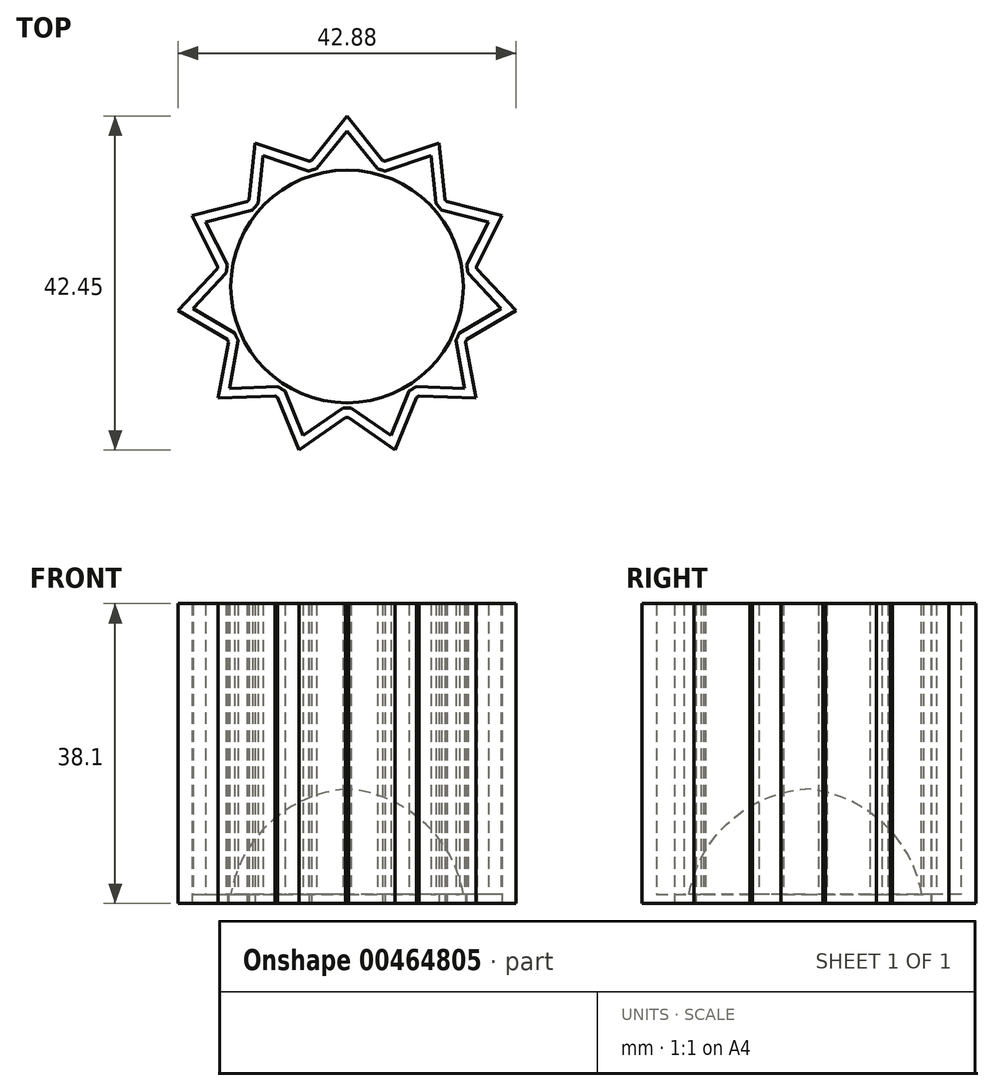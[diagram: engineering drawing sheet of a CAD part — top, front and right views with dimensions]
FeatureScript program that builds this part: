
annotation { "Feature Type Name" : "Feature", "Feature Type Description" : "" }
export const myFeature = defineFeature(function(context is Context, id is Id, definition is map)
    precondition{}
    {
        {
            var Q0;
            Q0=qCreatedBy(makeId("Top.planeOp"),FACE);
            var sketch = newSketch(context, id + "F0", { "sketchPlane" : qUnion([Q0])});
            skCircle(sketch, "E0", {"center": v(0, 0) * mm, "radius": 15.88 * mm, "construction": true});
            skCircle(sketch, "E1.0", {"center": v(0, 0) * mm, "radius": 16.64 * mm});
            skLineSegment(sketch, "E2", {"start": v(0, 0) * mm, "end": v(0, 21) * mm, "construction": true});
            skLineSegment(sketch, "E3", {"start": v(0, 21.66) * mm, "end": v(4.53, 16) * mm});
            skLineSegment(sketch, "E4.MirrorCS", {"start": v(0, 21.66) * mm, "end": v(-4.53, 16) * mm});
            skLineSegment(sketch, "E5.1.0", {"start": v(-11.71, 18.22) * mm, "end": v(-4.84, 15.92) * mm});
            skLineSegment(sketch, "E5.1.1", {"start": v(-11.71, 18.22) * mm, "end": v(-12.47, 11.02) * mm});
            skLineSegment(sketch, "E5.2.0", {"start": v(-19.7, 9) * mm, "end": v(-12.68, 10.77) * mm});
            skLineSegment(sketch, "E5.2.1", {"start": v(-19.7, 9) * mm, "end": v(-16.44, 2.53) * mm});
            skLineSegment(sketch, "E5.3.0", {"start": v(-21.44, -3.08) * mm, "end": v(-16.5, 2.2) * mm});
            skLineSegment(sketch, "E5.3.1", {"start": v(-21.44, -3.08) * mm, "end": v(-15.2, -6.76) * mm});
            skLineSegment(sketch, "E5.4.0", {"start": v(-16.37, -14.19) * mm, "end": v(-15.06, -7.06) * mm});
            skLineSegment(sketch, "E5.4.1", {"start": v(-16.37, -14.19) * mm, "end": v(-9.13, -13.9) * mm});
            skLineSegment(sketch, "E5.5.0", {"start": v(-6.1, -20.79) * mm, "end": v(-8.86, -14.08) * mm});
            skLineSegment(sketch, "E5.5.1", {"start": v(-6.1, -20.79) * mm, "end": v(-0.16, -16.64) * mm});
            skLineSegment(sketch, "E5.6.0", {"start": v(6.1, -20.79) * mm, "end": v(0.16, -16.64) * mm});
            skLineSegment(sketch, "E5.6.1", {"start": v(6.1, -20.79) * mm, "end": v(8.86, -14.08) * mm});
            skLineSegment(sketch, "E5.7.0", {"start": v(16.37, -14.19) * mm, "end": v(9.13, -13.9) * mm});
            skLineSegment(sketch, "E5.7.1", {"start": v(16.37, -14.19) * mm, "end": v(15.06, -7.06) * mm});
            skLineSegment(sketch, "E5.8.0", {"start": v(21.44, -3.08) * mm, "end": v(15.2, -6.76) * mm});
            skLineSegment(sketch, "E5.8.1", {"start": v(21.44, -3.08) * mm, "end": v(16.5, 2.2) * mm});
            skLineSegment(sketch, "E5.9.0", {"start": v(19.7, 9) * mm, "end": v(16.44, 2.53) * mm});
            skLineSegment(sketch, "E5.9.1", {"start": v(19.7, 9) * mm, "end": v(12.68, 10.77) * mm});
            skLineSegment(sketch, "E5.10.0", {"start": v(11.71, 18.22) * mm, "end": v(12.47, 11.02) * mm});
            skLineSegment(sketch, "E5.10.1", {"start": v(11.71, 18.22) * mm, "end": v(4.84, 15.92) * mm});
            skSolve(sketch);
        }
        {
            var Q0;
            Q0 = qSketchRegion(id + "F0", true);
            extrude(context, id + "F1", {"entities" : qUnion([Q0]), "depth" : 38.1 * mm});
        }
        {
            var Q0;
            Q0=makeQuery(id+"F1.opExtrude","CAP_FACE",FACE,{"disambiguationData":[OSD([sQuery(id+"F0.wireOp",EDGE,"E3"),sQuery(id+"F0.wireOp",EDGE,"E4.MirrorCS"),sQuery(id+"F0.wireOp",EDGE,"E5.1.0"),sQuery(id+"F0.wireOp",EDGE,"E5.1.1"),sQuery(id+"F0.wireOp",EDGE,"E5.2.0"),sQuery(id+"F0.wireOp",EDGE,"E5.2.1"),sQuery(id+"F0.wireOp",EDGE,"E5.3.0"),sQuery(id+"F0.wireOp",EDGE,"E5.3.1"),sQuery(id+"F0.wireOp",EDGE,"E5.4.0"),sQuery(id+"F0.wireOp",EDGE,"E5.4.1"),sQuery(id+"F0.wireOp",EDGE,"E5.5.0"),sQuery(id+"F0.wireOp",EDGE,"E5.5.1"),sQuery(id+"F0.wireOp",EDGE,"E5.6.0"),sQuery(id+"F0.wireOp",EDGE,"E5.6.1"),sQuery(id+"F0.wireOp",EDGE,"E5.7.0"),sQuery(id+"F0.wireOp",EDGE,"E5.7.1"),sQuery(id+"F0.wireOp",EDGE,"E5.8.0"),sQuery(id+"F0.wireOp",EDGE,"E5.8.1"),sQuery(id+"F0.wireOp",EDGE,"E5.9.0"),sQuery(id+"F0.wireOp",EDGE,"E5.9.1"),sQuery(id+"F0.wireOp",EDGE,"E5.10.0"),sQuery(id+"F0.wireOp",EDGE,"E5.10.1"),sQuery(id+"F0.wireOp",EDGE,"E1.0")])],"isStart":false});
            shell(context, id + "F2", {"entities" : qUnion([Q0]), "thickness" : 1.2 * mm});
        }
        {
            var Q0;
            Q0=qCreatedBy(makeId("Front.planeOp"),FACE);
            var sketch = newSketch(context, id + "F3", { "sketchPlane" : qUnion([Q0])});
            skLineSegment(sketch, "E6.0", {"start": v(5.57, 1.2) * mm, "end": v(0.53, 1.2) * mm, "construction": true});
            skLineSegment(sketch, "E7.0", {"start": v(-0.53, 1.2) * mm, "end": v(0.53, 1.2) * mm, "construction": true});
            skLineSegment(sketch, "E8.0", {"start": v(0, 38.1) * mm, "end": v(0, 1.2) * mm});
            skArc(sketch, "E9", {"start": v(14.77, 1.2) * mm, "mid": v(9.67, 10.4) * mm, "end": v(0, 14.55) * mm});
            skLineSegment(sketch, "E10", {"start": v(0, 14.55) * mm, "end": v(0, 1.2) * mm});
            skLineSegment(sketch, "E11", {"start": v(14.77, 1.2) * mm, "end": v(0, 1.2) * mm});
            skPoint(sketch, "E12.0.start.orphan", {"position": v(19.55, 38.1) * mm});
            skSolve(sketch);
        }
        {
            var Q0;
            Q0 = qSketchRegion(id + "F3", true);
            var Q1;
            Q1=sQuery(id+"F3.wireOp",EDGE,"E8.0");
            revolve(context, id + "F4", {"operationType" : NewBodyOperationType.ADD, "entities" : qUnion([Q0]), "axis" : qUnion([Q1]), "revolveType" : RevolveType.FULL});
        }
    });
